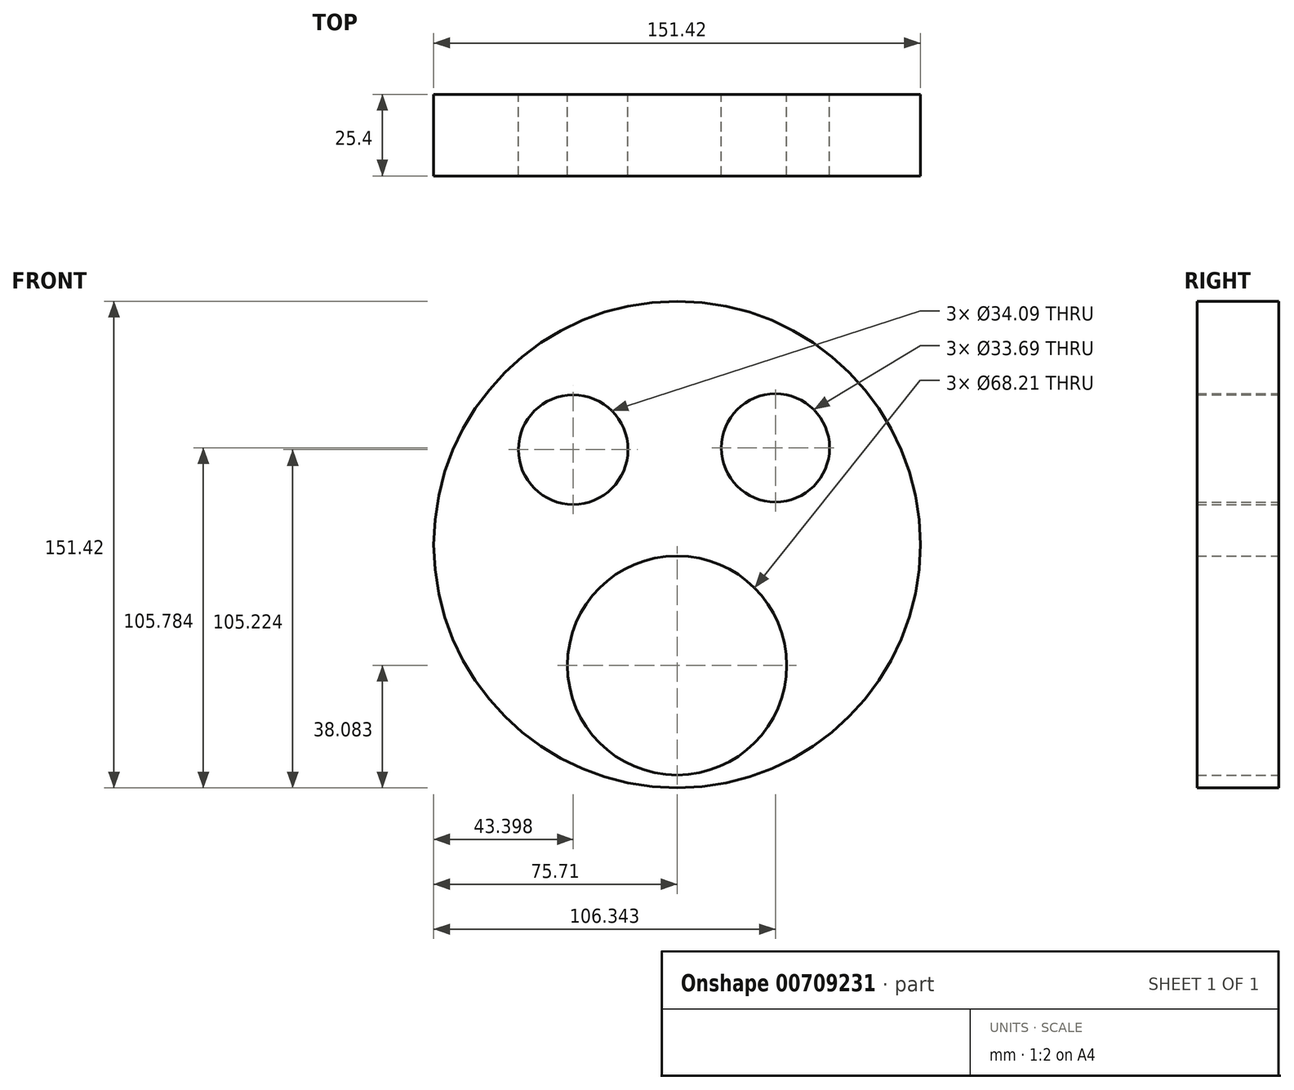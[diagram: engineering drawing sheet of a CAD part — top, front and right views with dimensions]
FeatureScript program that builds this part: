
annotation { "Feature Type Name" : "Feature", "Feature Type Description" : "" }
export const myFeature = defineFeature(function(context is Context, id is Id, definition is map)
    precondition{}
    {
        {
            var Q0;
            Q0=qCreatedBy(makeId("Front.planeOp"),FACE);
            var sketch = newSketch(context, id + "F0", { "sketchPlane" : qUnion([Q0])});
            skCircle(sketch, "E0", {"center": v(0, 0) * mm, "radius": 75.71 * mm});
            skCircle(sketch, "E1", {"center": v(-32.31, 29.51) * mm, "radius": 17.04 * mm});
            skCircle(sketch, "E2", {"center": v(30.63, 30.07) * mm, "radius": 16.84 * mm});
            skCircle(sketch, "E3", {"center": v(0, -37.63) * mm, "radius": 34.1 * mm});
            skSolve(sketch);
        }
        {
            var Q0;
            Q0 = qSketchRegion(id + "F0", true);
            extrude(context, id + "F1", {"entities" : qUnion([Q0]), "depth" : 25.4 * mm, "offsetDistance" : 25.4 * mm});
        }
    });
